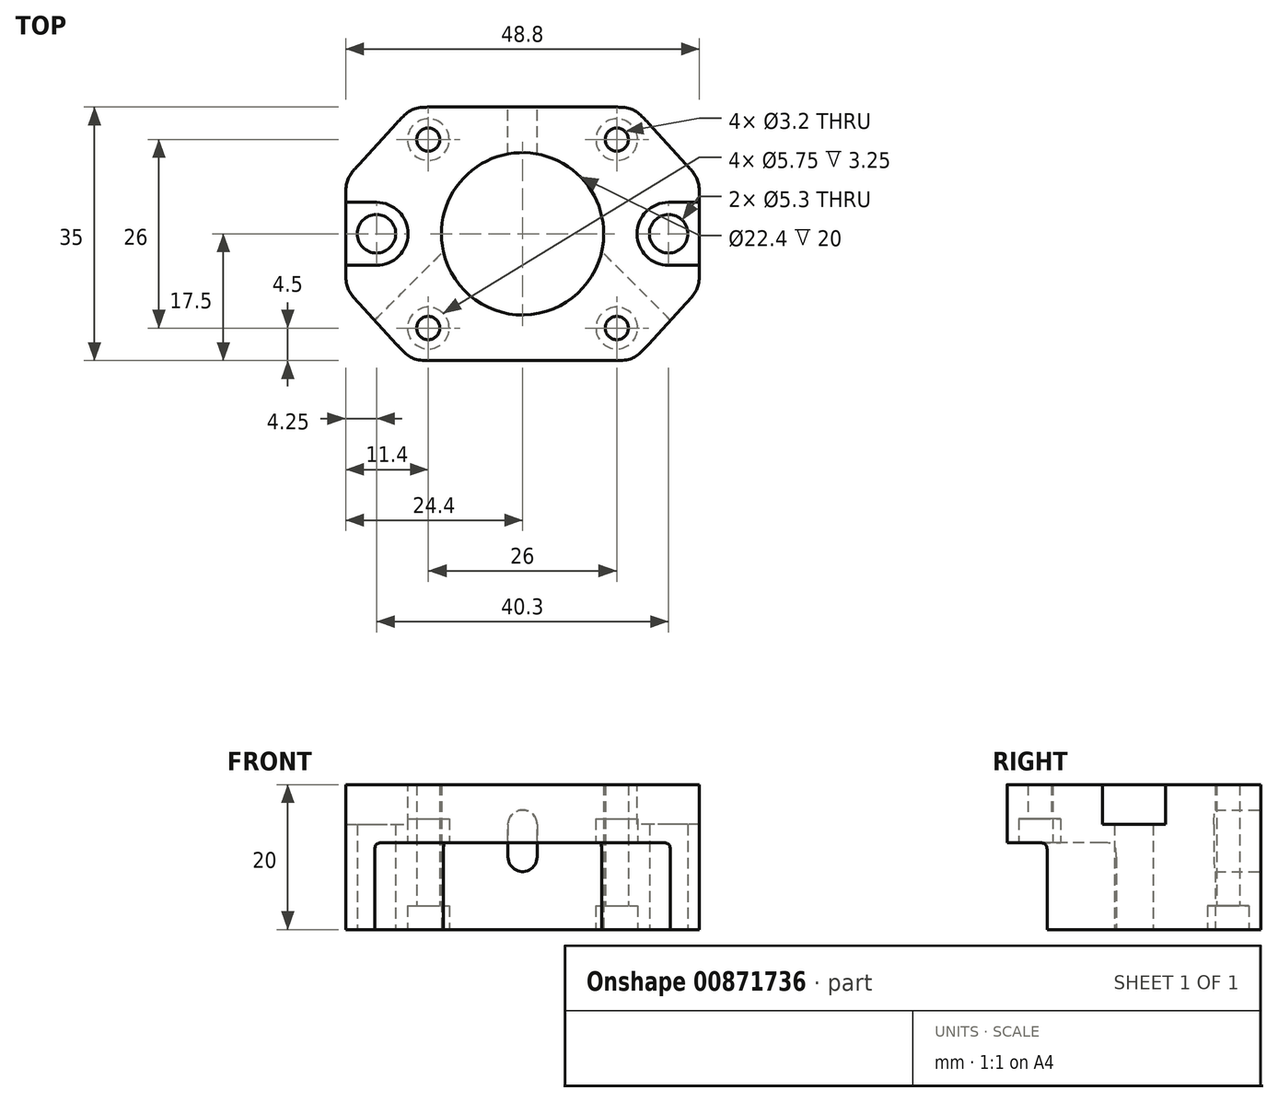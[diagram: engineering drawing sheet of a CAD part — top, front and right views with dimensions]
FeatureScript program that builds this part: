
annotation { "Feature Type Name" : "Feature", "Feature Type Description" : "" }
export const myFeature = defineFeature(function(context is Context, id is Id, definition is map)
    precondition{}
    {
        {
            var Q0;
            Q0=qCreatedBy(makeId("Top.planeOp"),FACE);
            var sketch = newSketch(context, id + "F0", { "sketchPlane" : qUnion([Q0])});
            skLineSegment(sketch, "E0.bottom", {"start": v(17.5, 17.5) * mm, "end": v(-17.5, 17.5) * mm});
            skLineSegment(sketch, "E0.top", {"start": v(17.5, -17.5) * mm, "end": v(-17.5, -17.5) * mm});
            skLineSegment(sketch, "E0.left", {"start": v(17.5, 17.5) * mm, "end": v(17.5, -17.5) * mm});
            skLineSegment(sketch, "E0.right", {"start": v(-17.5, 17.5) * mm, "end": v(-17.5, -17.5) * mm});
            skPoint(sketch, "E0.middle", {"position": v(0, 0) * mm});
            skCircle(sketch, "E1", {"center": v(0, 0) * mm, "radius": 23.25 * mm, "construction": true});
            skLineSegment(sketch, "E2.bottom", {"start": v(13, 13) * mm, "end": v(-13, 13) * mm, "construction": true});
            skLineSegment(sketch, "E2.top", {"start": v(13, -13) * mm, "end": v(-13, -13) * mm, "construction": true});
            skLineSegment(sketch, "E2.left", {"start": v(13, 13) * mm, "end": v(13, -13) * mm, "construction": true});
            skLineSegment(sketch, "E2.right", {"start": v(-13, 13) * mm, "end": v(-13, -13) * mm, "construction": true});
            skSolve(sketch);
        }
        {
            var Q0;
            Q0=qCreatedBy(makeId("Top.planeOp"),FACE);
            var sketch = newSketch(context, id + "F1", { "sketchPlane" : qUnion([Q0])});
            skLineSegment(sketch, "E3", {"start": v(0, 17.5) * mm, "end": v(15.3, 17.5) * mm});
            skLineSegment(sketch, "E4", {"start": v(15.3, -17.5) * mm, "end": v(0, -17.5) * mm});
            skCircle(sketch, "E5", {"center": v(20.15, 0) * mm, "radius": 2.65 * mm});
            skCircle(sketch, "E6", {"center": v(20.15, 0) * mm, "radius": 4.25 * mm, "construction": true});
            skLineSegment(sketch, "E7", {"start": v(0, 17.5) * mm, "end": v(0, 11.2) * mm});
            skCircle(sketch, "E8", {"center": v(13, 13) * mm, "radius": 1.6 * mm});
            skCircle(sketch, "E9", {"center": v(13, -13) * mm, "radius": 1.6 * mm});
            skLineSegment(sketch, "E10", {"start": v(0, -11.2) * mm, "end": v(0, -11.2) * mm});
            skLineSegment(sketch, "E11", {"start": v(0, 11.2) * mm, "end": v(0, -11.2) * mm, "construction": true});
            skArc(sketch, "E12", {"start": v(0, -11.2) * mm, "mid": v(11.2, 0) * mm, "end": v(0, 11.2) * mm});
            skLineSegment(sketch, "E13", {"start": v(0, -11.2) * mm, "end": v(0, -17.5) * mm});
            skLineSegment(sketch, "E14", {"start": v(15.3, -17.5) * mm, "end": v(24.4, -7.58) * mm});
            skLineSegment(sketch, "E15", {"start": v(24.4, -7.58) * mm, "end": v(24.4, 7.58) * mm});
            skLineSegment(sketch, "E16", {"start": v(24.4, 7.58) * mm, "end": v(15.3, 17.5) * mm});
            skSolve(sketch);
        }
        {
            var Q0;
            Q0 = qSketchRegion(id + "F1", true);
            extrude(context, id + "F2", {"entities" : qUnion([Q0]), "depth" : 20 * mm, "offsetDistance" : 25 * mm});
        }
        {
            var Q0;
            Q0=makeQuery(id+"F2.opExtrude","CAP_FACE",FACE,{"disambiguationData":[OSD([sQuery(id+"F1.wireOp",EDGE,"E3"),sQuery(id+"F1.wireOp",EDGE,"E4"),sQuery(id+"F1.wireOp",EDGE,"J8OLWbGK-Hipg-Fh6x-Z2FD-VSMyOfVtSBrD"),sQuery(id+"F1.wireOp",EDGE,"vRjLCx4a-CCAp-KVt6-0zQo-nvNLyXMbnnDs"),sQuery(id+"F1.wireOp",EDGE,"lvdZwN9g-rioz-ZCs0-Xke9-fPOytbawJhew"),sQuery(id+"F1.wireOp",EDGE,"ubyiIRmP-Zs37-gWBV-OHRN-k2AapoS8op0R"),sQuery(id+"F1.wireOp",EDGE,"E5"),sQuery(id+"F1.wireOp",EDGE,"6DK1e1tu-JMtU-CSTG-RR4p-xX76VrGJ2m3I"),sQuery(id+"F1.wireOp",EDGE,"E7"),sQuery(id+"F1.wireOp",EDGE,"E8"),sQuery(id+"F1.wireOp",EDGE,"E9"),sQuery(id+"F1.wireOp",EDGE,"E12"),sQuery(id+"F1.wireOp",EDGE,"E13")])],"isStart":false});
            var sketch = newSketch(context, id + "F3", { "sketchPlane" : qUnion([Q0])});
            skLineSegment(sketch, "E17", {"start": v(24.4, 4.35) * mm, "end": v(20.15, 4.35) * mm});
            skLineSegment(sketch, "E18", {"start": v(20.15, 4.35) * mm, "end": v(20.15, -4.35) * mm, "construction": true});
            skLineSegment(sketch, "E19", {"start": v(20.15, -4.35) * mm, "end": v(24.4, -4.35) * mm});
            skArc(sketch, "E20", {"start": v(20.15, 4.35) * mm, "mid": v(15.8, 0) * mm, "end": v(20.15, -4.35) * mm});
            skLineSegment(sketch, "E21.2", {"start": v(24.4, 4.35) * mm, "end": v(24.4, -4.35) * mm});
            skSolve(sketch);
        }
        {
            var Q0;
            Q0 = qSketchRegion(id + "F3", true);
            extrude(context, id + "F4", {"entities" : qUnion([Q0]), "operationType" : NewBodyOperationType.REMOVE, "oppositeDirection" : true, "depth" : 5.5 * mm, "offsetDistance" : 25 * mm});
        }
        {
            var Q0;
            Q0=makeQuery(id+"F2.opExtrude","SWEPT_EDGE",EDGE,{"disambiguationData":[OSD([sQuery(id+"F1.wireOp",EDGE,"cYioU41F-zUGK-qsMa-Fdf4-ZO7VMeL32mNc"),sQuery(id+"F1.wireOp",EDGE,"8K5GSUVV-BYPL-AxzQ-Y5Z7-b58ROFt6ySsB")])]});
            var Q1;
            Q1=makeQuery(id+"F2.opExtrude","SWEPT_EDGE",EDGE,{"disambiguationData":[OSD([sQuery(id+"F1.wireOp",EDGE,"cCU8ng39-XuzE-YR7Y-GhU2-kyD9zMTynqwV"),sQuery(id+"F1.wireOp",EDGE,"xHTAKdyR-LOUW-qOXc-cOtQ-MquGYUOO9mEh")])]});
            var Q2;
            Q2=makeQuery(id+"F2.opExtrude","SWEPT_EDGE",EDGE,{"disambiguationData":[OSD([sQuery(id+"F1.wireOp",EDGE,"E4"),sQuery(id+"F1.wireOp",EDGE,"E14")])]});
            var Q3;
            Q3=makeQuery(id+"F2.opExtrude","SWEPT_EDGE",EDGE,{"disambiguationData":[OSD([sQuery(id+"F1.wireOp",EDGE,"E14"),sQuery(id+"F1.wireOp",EDGE,"E15")])]});
            var Q4;
            Q4=makeQuery(id+"F2.opExtrude","SWEPT_EDGE",EDGE,{"disambiguationData":[OSD([sQuery(id+"F1.wireOp",EDGE,"E15"),sQuery(id+"F1.wireOp",EDGE,"E16")])]});
            var Q5;
            Q5=makeQuery(id+"F2.opExtrude","SWEPT_EDGE",EDGE,{"disambiguationData":[OSD([sQuery(id+"F1.wireOp",EDGE,"E3"),sQuery(id+"F1.wireOp",EDGE,"E16")])]});
            fillet(context, id + "F5", {"entities" : qUnion([Q0, Q1, Q2, Q3, Q4, Q5]), "radius" : 7 * mm, "tangentPropagation" : true, "rho" : .7, "crossSection" : FilletCrossSection.CONIC, "allowEdgeOverflow" : false});
        }
        {
            var Q0;
            Q0=makeQuery(id+"F2.opExtrude","CAP_FACE",FACE,{"disambiguationData":[OSD([sQuery(id+"F1.wireOp",EDGE,"E3"),sQuery(id+"F1.wireOp",EDGE,"E4"),sQuery(id+"F1.wireOp",EDGE,"J8OLWbGK-Hipg-Fh6x-Z2FD-VSMyOfVtSBrD"),sQuery(id+"F1.wireOp",EDGE,"vRjLCx4a-CCAp-KVt6-0zQo-nvNLyXMbnnDs"),sQuery(id+"F1.wireOp",EDGE,"lvdZwN9g-rioz-ZCs0-Xke9-fPOytbawJhew"),sQuery(id+"F1.wireOp",EDGE,"ubyiIRmP-Zs37-gWBV-OHRN-k2AapoS8op0R"),sQuery(id+"F1.wireOp",EDGE,"E5"),sQuery(id+"F1.wireOp",EDGE,"6DK1e1tu-JMtU-CSTG-RR4p-xX76VrGJ2m3I"),sQuery(id+"F1.wireOp",EDGE,"E7"),sQuery(id+"F1.wireOp",EDGE,"E8"),sQuery(id+"F1.wireOp",EDGE,"E9"),sQuery(id+"F1.wireOp",EDGE,"E12"),sQuery(id+"F1.wireOp",EDGE,"E13")])],"isStart":true});
            var sketch = newSketch(context, id + "F6", { "sketchPlane" : qUnion([Q0])});
            skLineSegment(sketch, "E22", {"start": v(0, 17.5) * mm, "end": v(25.99, 17.5) * mm});
            skCircle(sketch, "E23", {"center": v(0, 0) * mm, "radius": 6 * mm, "construction": true});
            skLineSegment(sketch, "E24", {"start": v(25.99, 17.5) * mm, "end": v(4.24, -4.24) * mm});
            skLineSegment(sketch, "E25", {"start": v(4.24, -4.24) * mm, "end": v(0, -4.24) * mm});
            skLineSegment(sketch, "E26", {"start": v(0, -4.24) * mm, "end": v(0, 17.5) * mm});
            skSolve(sketch);
        }
        {
            var Q0;
            Q0 = qSketchRegion(id + "F6", true);
            extrude(context, id + "F7", {"entities" : qUnion([Q0]), "operationType" : NewBodyOperationType.REMOVE, "oppositeDirection" : true, "depth" : 12 * mm, "offsetDistance" : 25 * mm});
        }
        {
            var Q0;
            Q0=makeQuery(id+"F7.boolean.opBoolean","COPY",EDGE,{"derivedFrom":makeQuery(id+"F7.opExtrude","CAP_EDGE",EDGE,{"disambiguationData":[OSD([sQuery(id+"F6.wireOp",EDGE,"E24")])],"isStart":false})});
            fillet(context, id + "F8", {"entities" : qUnion([Q0]), "radius" : 2 * mm, "tangentPropagation" : true, "rho" : .7, "crossSection" : FilletCrossSection.CONIC, "allowEdgeOverflow" : false});
        }
        {
            var Q0;
            Q0=makeQuery(id+"F2.opExtrude","SWEPT_BODY",BODY,{"disambiguationData":[OSD([sQuery(id+"F1.wireOp",EDGE,"E3"),sQuery(id+"F1.wireOp",EDGE,"E4"),sQuery(id+"F1.wireOp",EDGE,"J8OLWbGK-Hipg-Fh6x-Z2FD-VSMyOfVtSBrD"),sQuery(id+"F1.wireOp",EDGE,"vRjLCx4a-CCAp-KVt6-0zQo-nvNLyXMbnnDs"),sQuery(id+"F1.wireOp",EDGE,"lvdZwN9g-rioz-ZCs0-Xke9-fPOytbawJhew"),sQuery(id+"F1.wireOp",EDGE,"ubyiIRmP-Zs37-gWBV-OHRN-k2AapoS8op0R"),sQuery(id+"F1.wireOp",EDGE,"E5"),sQuery(id+"F1.wireOp",EDGE,"6DK1e1tu-JMtU-CSTG-RR4p-xX76VrGJ2m3I"),sQuery(id+"F1.wireOp",EDGE,"E7"),sQuery(id+"F1.wireOp",EDGE,"E8"),sQuery(id+"F1.wireOp",EDGE,"E9"),sQuery(id+"F1.wireOp",EDGE,"E12"),sQuery(id+"F1.wireOp",EDGE,"E13")])]});
            var Q1;
            Q1=makeQuery(id+"F2.opExtrude","SWEPT_FACE",FACE,{"disambiguationData":[OSD([sQuery(id+"F1.wireOp",EDGE,"E7")])]});
            mirror(context, id + "F9", {"operationType" : NewBodyOperationType.ADD, "entities" : qUnion([Q0]), "mirrorPlane" : qUnion([Q1])});
        }
        {
            var Q0;
            {var subQ0=makeQuery(id+"F2.opExtrude","SWEPT_FACE",FACE,{"disambiguationData":[OSD([sQuery(id+"F1.wireOp",EDGE,"E3")])]});Q0=makeQuery(id+"F9.boolean.opBoolean","MERGE",FACE,{"derivedFrom":[subQ0,makeQuery(id+"F9.opPattern","COPY",FACE,{"derivedFrom":subQ0,"instanceName":"1"})]});}
            var sketch = newSketch(context, id + "F10", { "sketchPlane" : qUnion([Q0])});
            skLineSegment(sketch, "E27.bottom", {"start": v(-2, 10) * mm, "end": v(2, 10) * mm, "construction": true});
            skLineSegment(sketch, "E27.top", {"start": v(-2, 14.5) * mm, "end": v(2, 14.5) * mm, "construction": true});
            skLineSegment(sketch, "E27.left", {"start": v(-2, 10) * mm, "end": v(-2, 14.5) * mm});
            skLineSegment(sketch, "E27.right", {"start": v(2, 10) * mm, "end": v(2, 14.5) * mm});
            skPoint(sketch, "E27.middle", {"position": v(0, 12.25) * mm});
            skArc(sketch, "E28", {"start": v(-2, 10) * mm, "mid": v(0, 8) * mm, "end": v(2, 10) * mm});
            skArc(sketch, "E29", {"start": v(2, 14.5) * mm, "mid": v(0, 16.5) * mm, "end": v(-2, 14.5) * mm});
            skLineSegment(sketch, "E30", {"start": v(0, 16.5) * mm, "end": v(0, 20) * mm, "construction": true});
            skPoint(sketch, "E31.endSnap0", {"position": v(0, 8) * mm});
            skLineSegment(sketch, "E32", {"start": v(0, 8) * mm, "end": v(0, 0) * mm, "construction": true});
            skSolve(sketch);
        }
        {
            var Q0;
            Q0 = qSketchRegion(id + "F10", true);
            extrude(context, id + "F11", {"entities" : qUnion([Q0]), "operationType" : NewBodyOperationType.REMOVE, "endBound" : BoundingType.UP_TO_NEXT, "oppositeDirection" : true, "depth" : 25 * mm, "offsetDistance" : 25 * mm});
        }
        {
            var Q0;
            {var subQ0=makeQuery(id+"F7.boolean.opBoolean","COPY",FACE,{"derivedFrom":makeQuery(id+"F7.opExtrude","CAP_FACE",FACE,{"disambiguationData":[OSD([sQuery(id+"F6.wireOp",EDGE,"lww8rJte-HnX0-tJqf-Jg64-2pbPNw81bPG2"),sQuery(id+"F6.wireOp",EDGE,"E22"),sQuery(id+"F6.wireOp",EDGE,"opBByrwI-z1QE-ruTP-V73B-DmUWUIDapPBD")])],"isStart":false})});Q0=makeQuery(id+"F9.boolean.opBoolean","MERGE",FACE,{"derivedFrom":[subQ0,makeQuery(id+"F9.opPattern","COPY",FACE,{"derivedFrom":subQ0,"instanceName":"1"})]});}
            var sketch = newSketch(context, id + "F12", { "sketchPlane" : qUnion([Q0])});
            skCircle(sketch, "E33", {"center": v(13, 13) * mm, "radius": 2.88 * mm});
            skCircle(sketch, "E34", {"center": v(-13, 13) * mm, "radius": 2.88 * mm});
            skCircle(sketch, "E35", {"center": v(-13, -13) * mm, "radius": 2.88 * mm, "construction": true});
            skCircle(sketch, "E36", {"center": v(13, -13) * mm, "radius": 2.88 * mm, "construction": true});
            skLineSegment(sketch, "E37", {"start": v(-13, 13) * mm, "end": v(-13, 15.88) * mm, "construction": true});
            skLineSegment(sketch, "E38", {"start": v(-13, 15.88) * mm, "end": v(-13, 17.5) * mm, "construction": true});
            skSolve(sketch);
        }
        {
            var Q0;
            Q0 = qSketchRegion(id + "F12", true);
            extrude(context, id + "F13", {"entities" : qUnion([Q0]), "operationType" : NewBodyOperationType.REMOVE, "oppositeDirection" : true, "depth" : 3.25 * mm, "offsetDistance" : 25 * mm});
        }
        {
            var Q0;
            {var subQ0=makeQuery(id+"F2.opExtrude","CAP_FACE",FACE,{"disambiguationData":[OSD([sQuery(id+"F1.wireOp",EDGE,"E3"),sQuery(id+"F1.wireOp",EDGE,"E4"),sQuery(id+"F1.wireOp",EDGE,"lvdZwN9g-rioz-ZCs0-Xke9-fPOytbawJhew"),sQuery(id+"F1.wireOp",EDGE,"ubyiIRmP-Zs37-gWBV-OHRN-k2AapoS8op0R"),sQuery(id+"F1.wireOp",EDGE,"E5"),sQuery(id+"F1.wireOp",EDGE,"6DK1e1tu-JMtU-CSTG-RR4p-xX76VrGJ2m3I"),sQuery(id+"F1.wireOp",EDGE,"E7"),sQuery(id+"F1.wireOp",EDGE,"E8"),sQuery(id+"F1.wireOp",EDGE,"E9"),sQuery(id+"F1.wireOp",EDGE,"E12"),sQuery(id+"F1.wireOp",EDGE,"E13"),sQuery(id+"F1.wireOp",EDGE,"cYioU41F-zUGK-qsMa-Fdf4-ZO7VMeL32mNc"),sQuery(id+"F1.wireOp",EDGE,"8K5GSUVV-BYPL-AxzQ-Y5Z7-b58ROFt6ySsB"),sQuery(id+"F1.wireOp",EDGE,"cCU8ng39-XuzE-YR7Y-GhU2-kyD9zMTynqwV"),sQuery(id+"F1.wireOp",EDGE,"xHTAKdyR-LOUW-qOXc-cOtQ-MquGYUOO9mEh")])],"isStart":true});Q0=makeQuery(id+"F9.boolean.opBoolean","MERGE",FACE,{"derivedFrom":[subQ0,makeQuery(id+"F9.opPattern","COPY",FACE,{"derivedFrom":subQ0,"instanceName":"1"})]});}
            var sketch = newSketch(context, id + "F14", { "sketchPlane" : qUnion([Q0])});
            skCircle(sketch, "E39", {"center": v(13, -13) * mm, "radius": 2.88 * mm});
            skCircle(sketch, "E40", {"center": v(-13, -13) * mm, "radius": 2.88 * mm});
            skSolve(sketch);
        }
        {
            var Q0;
            Q0 = qSketchRegion(id + "F14", true);
            extrude(context, id + "F15", {"entities" : qUnion([Q0]), "operationType" : NewBodyOperationType.REMOVE, "oppositeDirection" : true, "depth" : 3.25 * mm, "offsetDistance" : 25 * mm});
        }
    });
